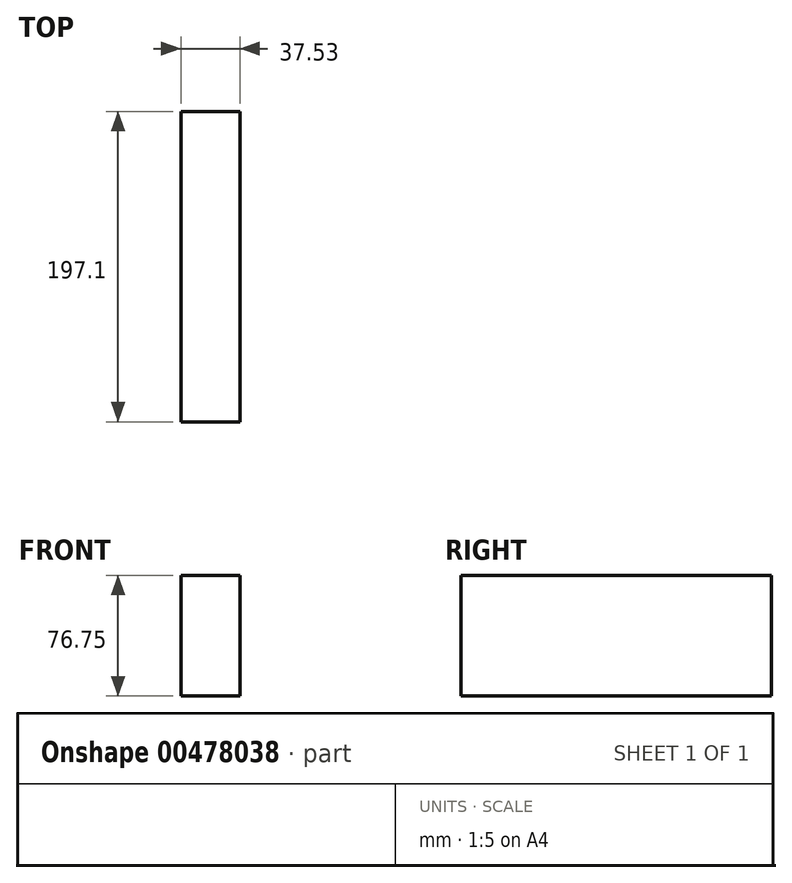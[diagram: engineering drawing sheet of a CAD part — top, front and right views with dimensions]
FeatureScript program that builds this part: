
annotation { "Feature Type Name" : "Feature", "Feature Type Description" : "" }
export const myFeature = defineFeature(function(context is Context, id is Id, definition is map)
    precondition{}
    {
        {
            var Q0;
            Q0=qCreatedBy(makeId("Front.planeOp"),FACE);
            var sketch = newSketch(context, id + "F0", { "sketchPlane" : qUnion([Q0])});
            skLineSegment(sketch, "E0.bottom", {"start": v(0, 0) * mm, "end": v(-37.53, 0) * mm});
            skLineSegment(sketch, "E0.top", {"start": v(0, 76.75) * mm, "end": v(-37.53, 76.75) * mm});
            skLineSegment(sketch, "E0.left", {"start": v(0, 0) * mm, "end": v(0, 76.75) * mm});
            skLineSegment(sketch, "E0.right", {"start": v(-37.53, 0) * mm, "end": v(-37.53, 76.75) * mm});
            skSolve(sketch);
        }
        {
            var Q0;
            Q0 = qSketchRegion(id + "F0", true);
            extrude(context, id + "F1", {"entities" : qUnion([Q0]), "oppositeDirection" : true, "depth" : 197.1 * mm});
        }
        {
            var Q0;
            Q0=qCreatedBy(makeId("Front.planeOp"),FACE);
            var sketch = newSketch(context, id + "F2", { "sketchPlane" : qUnion([Q0])});
            skCircle(sketch, "E1", {"center": v(-66.8, 83.6) * mm, "radius": 23.58 * mm});
            skSolve(sketch);
        }
        {
            var Q0;
            Q0=makeQuery(id+"F2.imprint","IMPRINT",FACE,{"disambiguationData":[TD([[makeQuery(id+"F2.imprint","IMPRINT",EDGE,{"derivedFrom":sQuery(id+"F2.wireOp",EDGE,"E1")}),1.0]])]});
            var Q1;
            Q1=sQuery(id+"F2.wireOp",EDGE,"E1");
            extrude(context, id + "F3", {"entities" : qUnion([Q0]), "surfaceEntities" : qUnion([Q1]), "oppositeDirection" : true, "depth" : 196.34 * mm});
        }
        {
            var Q0;
            Q0=makeQuery(id+"F3.opExtrude","SWEPT_BODY",BODY,{"disambiguationData":[OSD([sQuery(id+"F2.wireOp",EDGE,"E1")])]});
            deleteBodies(context, id + "F4", {"entities" : qUnion([Q0])});
        }
    });
